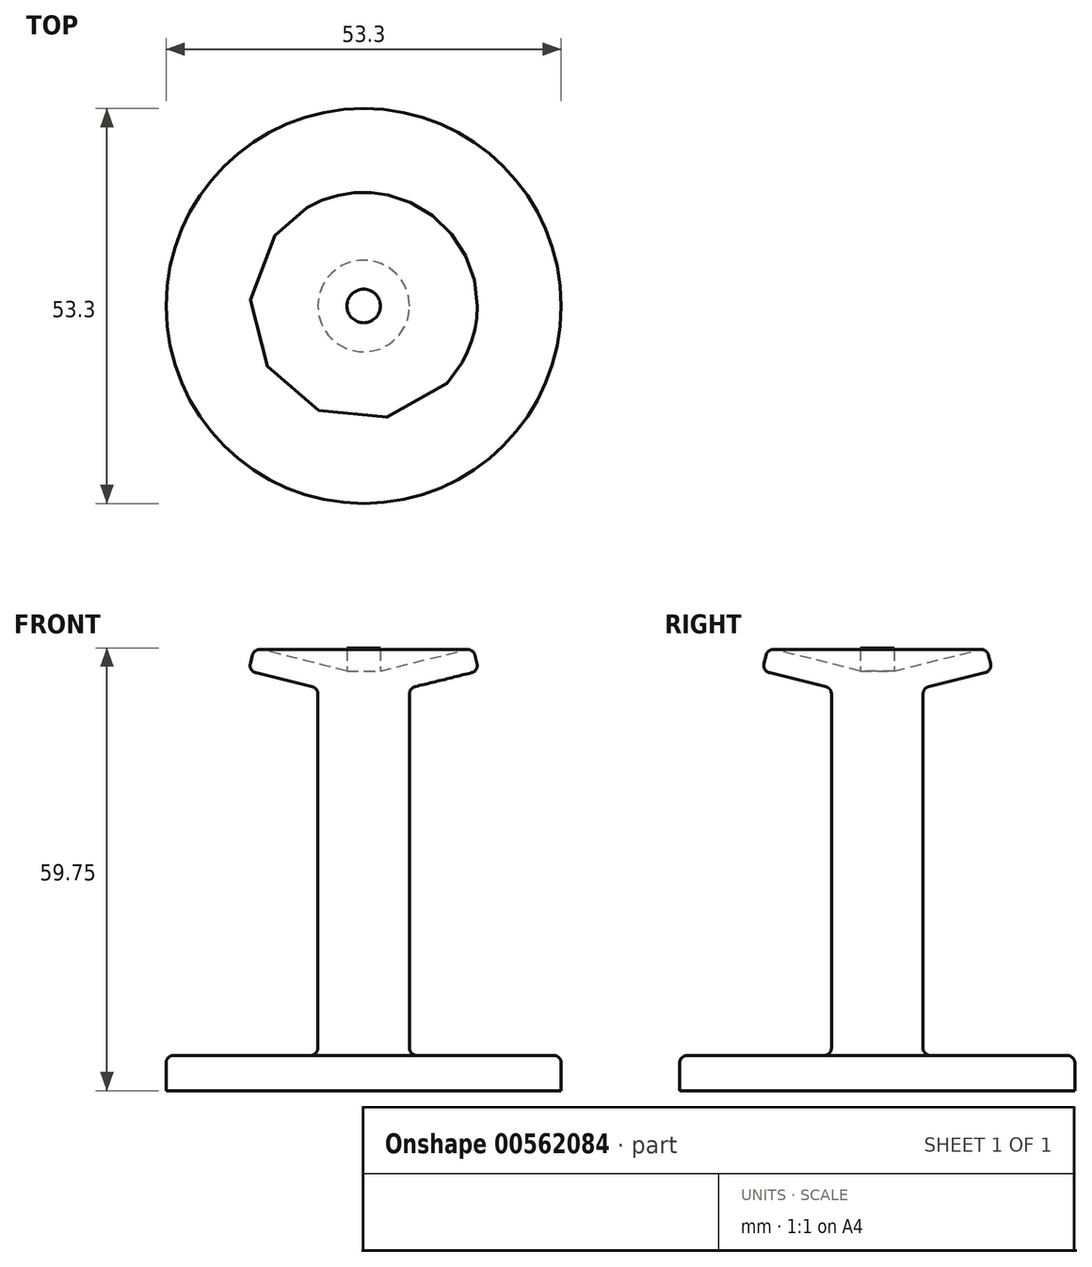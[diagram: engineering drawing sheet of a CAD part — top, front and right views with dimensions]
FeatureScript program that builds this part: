
annotation { "Feature Type Name" : "Feature", "Feature Type Description" : "" }
export const myFeature = defineFeature(function(context is Context, id is Id, definition is map)
    precondition{}
    {
        {
            var Q0;
            Q0=qCreatedBy(makeId("Front.planeOp"),FACE);
            var sketch = newSketch(context, id + "F0", { "sketchPlane" : qUnion([Q0])});
            skLineSegment(sketch, "E0", {"start": v(0, 0) * mm, "end": v(2.26, 0) * mm});
            skLineSegment(sketch, "E1", {"start": v(2.26, 0) * mm, "end": v(2.26, -3.1) * mm});
            skLineSegment(sketch, "E2", {"start": v(2.26, -3.1) * mm, "end": v(14.77, 0) * mm});
            skLineSegment(sketch, "E3", {"start": v(14.77, 0) * mm, "end": v(15.54, -3.1) * mm});
            skLineSegment(sketch, "E4", {"start": v(15.54, -3.1) * mm, "end": v(6.18, -5.42) * mm});
            skLineSegment(sketch, "E5", {"start": v(6.18, -5.42) * mm, "end": v(6.18, -55) * mm});
            skLineSegment(sketch, "E6", {"start": v(6.18, -55) * mm, "end": v(26.65, -55) * mm});
            skLineSegment(sketch, "E7", {"start": v(26.65, -55) * mm, "end": v(26.65, -59.75) * mm});
            skLineSegment(sketch, "E8", {"start": v(26.65, -59.75) * mm, "end": v(0, -59.75) * mm});
            skLineSegment(sketch, "E9", {"start": v(0, -59.75) * mm, "end": v(0, 0) * mm});
            skSolve(sketch);
        }
        {
            var Q0;
            Q0=makeQuery(id+"F0.imprint","IMPRINT",FACE,{"disambiguationData":[TD([[makeQuery(id+"F0.imprint","IMPRINT",EDGE,{"derivedFrom":sQuery(id+"F0.wireOp",EDGE,"E0")}),-1.0]])]});
            var Q1;
            Q1=sQuery(id+"F0.wireOp",EDGE,"E9");
            revolve(context, id + "F1", {"entities" : qUnion([Q0]), "axis" : qUnion([Q1]), "revolveType" : RevolveType.FULL});
        }
        {
            var Q0;
            Q0=makeQuery(id+"F1.opRevolve","SWEPT_EDGE",EDGE,{"disambiguationData":[OSD([sQuery(id+"F0.wireOp",EDGE,"E2"),sQuery(id+"F0.wireOp",EDGE,"E3")])]});
            var Q1;
            Q1=makeQuery(id+"F1.opRevolve","SWEPT_EDGE",EDGE,{"disambiguationData":[OSD([sQuery(id+"F0.wireOp",EDGE,"E3"),sQuery(id+"F0.wireOp",EDGE,"E4")])]});
            var Q2;
            Q2=makeQuery(id+"F1.opRevolve","SWEPT_EDGE",EDGE,{"disambiguationData":[OSD([sQuery(id+"F0.wireOp",EDGE,"E6"),sQuery(id+"F0.wireOp",EDGE,"E7")])]});
            var Q3;
            Q3=makeQuery(id+"F1.opRevolve","SWEPT_EDGE",EDGE,{"disambiguationData":[OSD([sQuery(id+"F0.wireOp",EDGE,"E5"),sQuery(id+"F0.wireOp",EDGE,"E6")])]});
            var Q4;
            Q4=makeQuery(id+"F1.opRevolve","SWEPT_EDGE",EDGE,{"disambiguationData":[OSD([sQuery(id+"F0.wireOp",EDGE,"E4"),sQuery(id+"F0.wireOp",EDGE,"E5")])]});
            fillet(context, id + "F2", {"entities" : qUnion([Q0, Q1, Q2, Q3, Q4]), "radius" : 1 * mm, "tangentPropagation" : true, "allowEdgeOverflow" : false});
        }
    });
